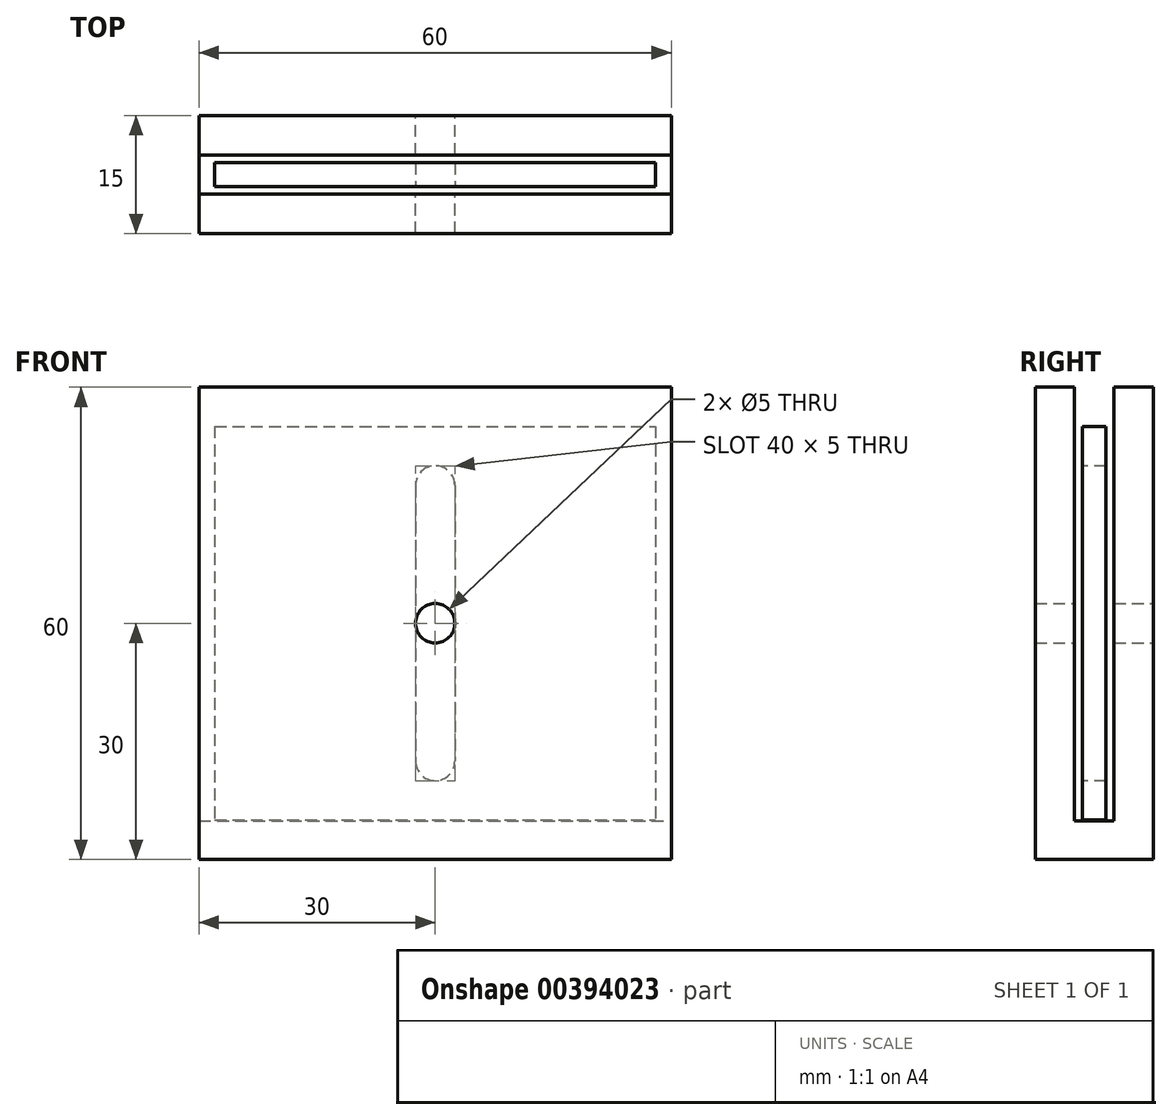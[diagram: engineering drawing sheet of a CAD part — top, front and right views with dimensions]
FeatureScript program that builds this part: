
annotation { "Feature Type Name" : "Feature", "Feature Type Description" : "" }
export const myFeature = defineFeature(function(context is Context, id is Id, definition is map)
    precondition{}
    {
        {
            var Q0;
            Q0=qCreatedBy(makeId("Front.planeOp"),FACE);
            var sketch = newSketch(context, id + "F0", { "sketchPlane" : qUnion([Q0])});
            skLineSegment(sketch, "E0.bottom", {"start": v(-28, 10) * mm, "end": v(28, 10) * mm});
            skLineSegment(sketch, "E0.top", {"start": v(-28, -40) * mm, "end": v(28, -40) * mm});
            skLineSegment(sketch, "E0.left", {"start": v(-28, 10) * mm, "end": v(-28, -40) * mm});
            skLineSegment(sketch, "E0.right", {"start": v(28, 10) * mm, "end": v(28, -40) * mm});
            skSolve(sketch);
        }
        {
            var Q0;
            Q0 = qSketchRegion(id + "F0", true);
            extrude(context, id + "F1", {"entities" : qUnion([Q0]), "endBound" : BoundingType.SYMMETRIC, "depth" : 3 * mm});
        }
        {
            var Q0;
            Q0=makeQuery(id+"F1.opExtrude","CAP_FACE",FACE,{"disambiguationData":[OSD([sQuery(id+"F0.wireOp",EDGE,"E0.bottom"),sQuery(id+"F0.wireOp",EDGE,"E0.top"),sQuery(id+"F0.wireOp",EDGE,"E0.left"),sQuery(id+"F0.wireOp",EDGE,"E0.right")])],"isStart":false});
            var sketch = newSketch(context, id + "F2", { "sketchPlane" : qUnion([Q0])});
            skCircle(sketch, "E1", {"center": v(0, 2.5) * mm, "radius": 2.5 * mm});
            skCircle(sketch, "E2", {"center": v(0, -32.5) * mm, "radius": 2.5 * mm});
            skLineSegment(sketch, "E3.bottom", {"start": v(2.5, 2.5) * mm, "end": v(-2.5, 2.5) * mm});
            skLineSegment(sketch, "E3.top", {"start": v(2.5, -32.5) * mm, "end": v(-2.5, -32.5) * mm});
            skLineSegment(sketch, "E3.left", {"start": v(2.5, 2.5) * mm, "end": v(2.5, -32.5) * mm});
            skLineSegment(sketch, "E3.right", {"start": v(-2.5, 2.5) * mm, "end": v(-2.5, -32.5) * mm});
            skSolve(sketch);
        }
        {
            var Q0;
            Q0 = qSketchRegion(id + "F2", true);
            extrude(context, id + "F3", {"entities" : qUnion([Q0]), "operationType" : NewBodyOperationType.REMOVE, "oppositeDirection" : true, "depth" : 25 * mm});
        }
        {
            var Q0;
            Q0=qCreatedBy(makeId("Front.planeOp"),FACE);
            cPlane(context, id + "F4", {"entities" : qUnion([Q0]), "cplaneType" : CPlaneType.OFFSET, "offset" : 5 * mm, "width" : 150 * mm, "height" : 150 * mm});
        }
        {
            var Q0;
            Q0=qCreatedBy(id+"F4.planeOp",FACE);
            var sketch = newSketch(context, id + "F5", { "sketchPlane" : qUnion([Q0])});
            skLineSegment(sketch, "E4.bottom", {"start": v(30, -45) * mm, "end": v(-30, -45) * mm});
            skLineSegment(sketch, "E4.top", {"start": v(30, 15) * mm, "end": v(-30, 15) * mm});
            skLineSegment(sketch, "E4.left", {"start": v(30, -45) * mm, "end": v(30, 15) * mm});
            skLineSegment(sketch, "E4.right", {"start": v(-30, -45) * mm, "end": v(-30, 15) * mm});
            skSolve(sketch);
        }
        {
            var Q0;
            Q0 = qSketchRegion(id + "F5", true);
            extrude(context, id + "F6", {"entities" : qUnion([Q0]), "endBound" : BoundingType.SYMMETRIC, "depth" : 5 * mm});
        }
        {
            var Q0;
            Q0=makeQuery(id+"F6.opExtrude","SWEPT_FACE",FACE,{"disambiguationData":[OSD([sQuery(id+"F5.wireOp",EDGE,"E4.bottom")])]});
            var sketch = newSketch(context, id + "F7", { "sketchPlane" : qUnion([Q0])});
            skLineSegment(sketch, "E5.bottom", {"start": v(-30, 7.5) * mm, "end": v(30, 7.5) * mm});
            skLineSegment(sketch, "E5.top", {"start": v(-30, -7.5) * mm, "end": v(30, -7.5) * mm});
            skLineSegment(sketch, "E5.left", {"start": v(-30, 7.5) * mm, "end": v(-30, -7.5) * mm});
            skLineSegment(sketch, "E5.right", {"start": v(30, 7.5) * mm, "end": v(30, -7.5) * mm});
            skSolve(sketch);
        }
        {
            var Q0;
            Q0 = qSketchRegion(id + "F7", true);
            extrude(context, id + "F8", {"entities" : qUnion([Q0]), "operationType" : NewBodyOperationType.ADD, "oppositeDirection" : true, "depth" : 4.9 * mm});
        }
        {
            var Q0;
            Q0=makeQuery(id+"F8.opExtrude","CAP_FACE",FACE,{"disambiguationData":[OSD([sQuery(id+"F7.wireOp",EDGE,"E5.bottom"),sQuery(id+"F7.wireOp",EDGE,"E5.top"),sQuery(id+"F7.wireOp",EDGE,"E5.left"),sQuery(id+"F7.wireOp",EDGE,"E5.right")])],"isStart":false});
            var sketch = newSketch(context, id + "F9", { "sketchPlane" : qUnion([Q0])});
            skLineSegment(sketch, "E6.bottom", {"start": v(30, 2.5) * mm, "end": v(-30, 2.5) * mm});
            skLineSegment(sketch, "E6.top", {"start": v(30, 7.5) * mm, "end": v(-30, 7.5) * mm});
            skLineSegment(sketch, "E6.left", {"start": v(30, 2.5) * mm, "end": v(30, 7.5) * mm});
            skLineSegment(sketch, "E6.right", {"start": v(-30, 2.5) * mm, "end": v(-30, 7.5) * mm});
            skSolve(sketch);
        }
        {
            var Q0;
            Q0 = qSketchRegion(id + "F9", true);
            extrude(context, id + "F10", {"entities" : qUnion([Q0]), "operationType" : NewBodyOperationType.ADD, "depth" : 55.1 * mm});
        }
        {
            var Q0;
            Q0=makeQuery(id+"F10.boolean.opBoolean","MERGE",FACE,{"derivedFrom":[makeQuery(id+"F8.opExtrude","SWEPT_FACE",FACE,{"disambiguationData":[OSD([sQuery(id+"F7.wireOp",EDGE,"E5.top")])]}),makeQuery(id+"F10.opExtrude","SWEPT_FACE",FACE,{"disambiguationData":[OSD([sQuery(id+"F9.wireOp",EDGE,"E6.top")])]})]});
            var sketch = newSketch(context, id + "F11", { "sketchPlane" : qUnion([Q0])});
            skCircle(sketch, "E7", {"center": v(0, -15) * mm, "radius": 2.5 * mm});
            skSolve(sketch);
        }
        {
            var Q0;
            Q0 = qSketchRegion(id + "F11", true);
            extrude(context, id + "F12", {"entities" : qUnion([Q0]), "operationType" : NewBodyOperationType.REMOVE, "oppositeDirection" : true, "depth" : 25 * mm});
        }
    });
